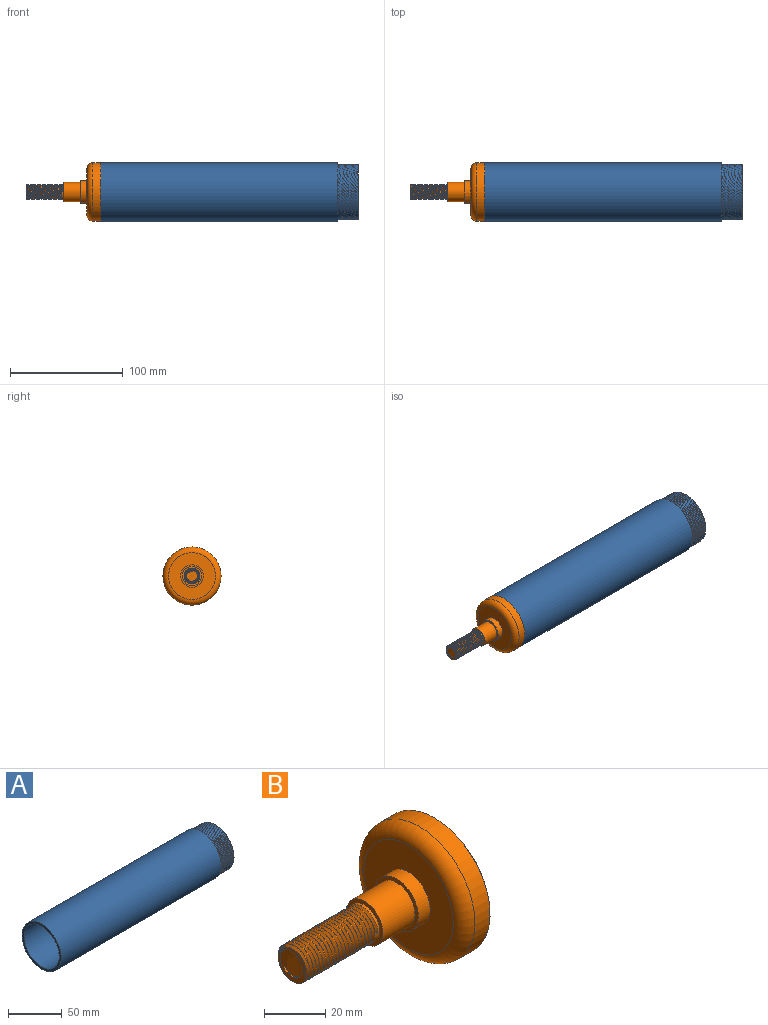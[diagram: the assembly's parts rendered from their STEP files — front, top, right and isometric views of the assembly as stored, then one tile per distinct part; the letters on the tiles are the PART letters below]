
ASSEMBLY  parts=2 mates=1
PART A: 13 faces, bbox 229x52.1x56.7 mm
  f0: cylinder r=23.6mm len=47.2mm, axis (-1,0,0), area 866.7mm2, adj f1,f7,f8,f9,f10,f11
  f1: plane 49.62x49.62mm, normal (1,0,0), area 115.3mm2, adj f0,f2,f8,f9
  f2: cylinder r=24.5mm len=49mm, axis (-1,0,0), area 2770.9mm2, adj f1,f3
  f3: plane 51.5x51.5mm, normal (1,0,0), area 197.3mm2, adj f2,f4
  f4: cylinder r=25.75mm len=210mm, axis (-1,0,0), area 33976.3mm2, adj f3,f5
  f5: plane 51.5x51.5mm, normal (-1,0,0), area 406.7mm2, adj f4,f6
  f6: cylinder r=23.1mm len=203mm, axis (-1,0,0), area 29463.7mm2, adj f5,f7
  f7: plane 47.2x47.2mm, normal (1,0,0), area 73.4mm2, adj f0,f6,f12
  f8: plane 0.69x0.4mm, normal (0,0,1), area 0.1mm2, adj f0,f1,f11
  f9: bspline ~56.1x48.59mm, area 2986.4mm2, adj f0,f1,f10,f11
  f10: plane 0.8x0.69mm, normal (0,0,-1), area 0.3mm2, adj f0,f9,f11,f12
  f11: bspline ~56.1x48.59mm, area 3001.2mm2, adj f0,f8,f9,f10,f12
  f12: cylinder r=23.6mm len=42.76mm, axis (-1,0,0), area 11.9mm2, adj f7,f10,f11
PART B: 46 faces, bbox 69.7x56.5x56.5 mm
  f0: plane 13.96x13.91mm, normal (-1,0,0), area 53.7mm2, adj f22,f23,f39,f40,f42,f45
  f1: cylinder r=7mm len=14mm, axis (-1,0,0), area 70.2mm2, adj f2,f37,f38,f39,f40
  f2: cylinder r=7mm len=14mm, axis (-1,0,0), area 5.6mm2, adj f1,f3,f39,f40
  f3: cylinder r=7mm len=14mm, axis (-1,0,0), area 5.6mm2, adj f2,f4,f39,f40
  f4: cylinder r=7mm len=14mm, axis (-1,0,0), area 5.6mm2, adj f3,f5,f39,f40
  f5: cylinder r=7mm len=14mm, axis (-1,0,0), area 5.6mm2, adj f4,f6,f39,f40
  f6: cylinder r=7mm len=14mm, axis (-1,0,0), area 5.6mm2, adj f5,f7,f39,f40
  f7: cylinder r=7mm len=14mm, axis (-1,0,0), area 5.7mm2, adj f6,f8,f39,f40
  f8: cylinder r=7mm len=14mm, axis (-1,0,0), area 5.7mm2, adj f7,f9,f39,f40
  f9: cylinder r=7mm len=14mm, axis (-1,0,0), area 5.7mm2, adj f8,f10,f39,f40
  f10: cylinder r=7mm len=14mm, axis (-1,0,0), area 5.6mm2, adj f9,f11,f39,f40
  f11: cylinder r=7mm len=14mm, axis (-1,0,0), area 5.6mm2, adj f10,f12,f39,f40
  f12: cylinder r=7mm len=14mm, axis (-1,0,0), area 5.6mm2, adj f11,f13,f39,f40
  f13: cylinder r=7mm len=14mm, axis (-1,0,0), area 5.7mm2, adj f12,f14,f39,f40
  f14: cylinder r=7mm len=14mm, axis (-1,0,0), area 5.6mm2, adj f13,f15,f39,f40
  f15: cylinder r=7mm len=14mm, axis (-1,0,0), area 5.6mm2, adj f14,f16,f39,f40
  f16: cylinder r=7mm len=14mm, axis (-1,0,0), area 5.7mm2, adj f15,f17,f39,f40
  f17: cylinder r=7mm len=14mm, axis (-1,0,0), area 5.7mm2, adj f16,f18,f39,f40
  f18: cylinder r=7mm len=14mm, axis (-1,0,0), area 5.7mm2, adj f17,f19,f39,f40
  f19: cylinder r=7mm len=14mm, axis (-1,0,0), area 5.6mm2, adj f18,f20,f39,f40
  f20: cylinder r=7mm len=14mm, axis (-1,0,0), area 5.6mm2, adj f19,f21,f39,f40
  f21: cylinder r=7mm len=14mm, axis (-1,0,0), area 5.6mm2, adj f20,f22,f39,f40
  f22: cylinder r=7mm len=14mm, axis (-1,0,0), area 3.7mm2, adj f0,f21,f39,f40
  f23: cylinder r=5mm len=33.6mm, axis (-1,0,0), area 190.3mm2, adj f0,f24,f42,f43,f44,f45
  f24: plane 10.01x10.01mm, normal (-1,0,0), area 50.3mm2, adj f23,f25,f41
  f25: cylinder r=3mm len=24.4mm, axis (-1,0,0), area 459.9mm2, adj f24,f26
  f26: plane 43x43mm, normal (1,0,0), area 1423.9mm2, adj f25,f27
  f27: cylinder r=21.5mm len=43mm, axis (-1,0,0), area 1350.9mm2, adj f26,f28
  f28: plane 46.2x46.2mm, normal (1,0,0), area 224.2mm2, adj f27,f29
  f29: cylinder r=23.1mm len=46.2mm, axis (-1,0,0), area 290.3mm2, adj f28,f30
  f30: plane 51.5x51.5mm, normal (1,0,0), area 406.7mm2, adj f29,f31
  f31: cylinder r=25.75mm len=51.5mm, axis (-1,0,0), area 1132.5mm2, adj f30,f32
  f32: torus R=20.75mm, axis (-1,0,0), area 1181.1mm2, adj f31,f33
  f33: plane 41.5x41.5mm, normal (-1,0,0), area 1038.5mm2, adj f32,f34
  f34: cylinder r=10mm len=20mm, axis (-1,0,0), area 345.6mm2, adj f33,f35
  f35: plane 20x20mm, normal (-1,0,0), area 87.2mm2, adj f34,f36
  f36: cylinder r=8.5mm len=17mm, axis (-1,0,0), area 795.8mm2, adj f35,f37
  f37: plane 17x17mm, normal (-1,0,0), area 73mm2, adj f1,f36
  f38: plane 1.37x0.96mm, normal (0,0.59,0.81), area 0.8mm2, adj f1,f39,f40
  f39: bspline ~33.2x16.13mm, area 985.9mm2, adj f0,f1,f2,f3,f4,f5,f6,f7
  f40: bspline ~33.7x16.13mm, area 1035.6mm2, adj f0,f1,f2,f3,f4,f5,f6,f7
  f41: bspline ~15.59x10mm, area 2.5mm2, adj f24,f43,f44
  f42: plane 0.69x0.4mm, normal (0,0,1), area 0.1mm2, adj f0,f23,f44
  f43: plane 0.8x0.56mm, normal (0,-0.59,0.81), area 0.3mm2, adj f23,f41,f44,f45
  f44: bspline ~34x11.14mm, area 789.2mm2, adj f23,f41,f42,f43,f45
  f45: bspline ~34x11.54mm, area 768.2mm2, adj f0,f23,f43,f44
PLACE A t=(-60.96,31.83,-42.53)mm
PLACE B t=(-60.96,31.83,-42.53)mm
MATE fastened A.f0 <-> B.f1  axis (-1,0,0) through (5.04,31.83,-42.53)mm
